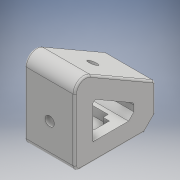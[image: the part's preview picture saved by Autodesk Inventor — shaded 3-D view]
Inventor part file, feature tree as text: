
AUTODESK INVENTOR PART (.ipt)
format: ipt  version: 2017 (Build 210142000, 142)  size: 297,472 bytes
history: native  units: mm
features: fillet x11, extrude x8, sketch x7, chamfer x2, other x1
ambient origin geometry x8: Origin, YZ Plane, XZ Plane, XY Plane, X Axis, Y Axis, Z Axis, Center Point
bodies: Body1 (feature_tree)
feature tree (29):
  other  "ソリッド1"
  extrude  "押し出し1"  Depth=24.0mm
  extrude  "押し出し2"  Depth=48.0mm
  extrude  "押し出し3"  Depth=28.0mm TaperAngle=0.0deg
  extrude  "押し出し4"  Depth=20.679492mm
  fillet  "フィレット1"  Radius=35.817931mm
  extrude  "押し出し7"  Depth=10.0mm
  extrude  "押し出し8"  Depth=10.0mm
  fillet  "フィレット2"  Radius=40.0mm
  fillet  "フィレット4"  Radius=14.0mm
  extrude  "押し出し9"  Depth=8.0mm
  extrude  "押し出し10"  Depth=20.679mm
  fillet  "フィレット6"  Radius=10.2mm
  fillet  "フィレット8"  Radius=14.2mm
  chamfer  "面取り1"  Distance=7.1mm
  fillet  "フィレット9"  Radius=5.1mm
  fillet  "フィレット10"  Radius=17.2mm
  fillet  "フィレット11"  Radius=8.5mm
  chamfer  "面取り3"  Distance=4.25mm
  fillet  "フィレット12"  Radius=8.6mm
  fillet  "フィレット13"  Radius=5.0mm
  fillet  "フィレット14"  Radius=8.0mm
  sketch  "スケッチ1"
  sketch  "スケッチ3"
  sketch  "スケッチ4"
  sketch  "スケッチ8"
  sketch  "スケッチ9"
  sketch  "スケッチ10"
  sketch  "スケッチ11"
